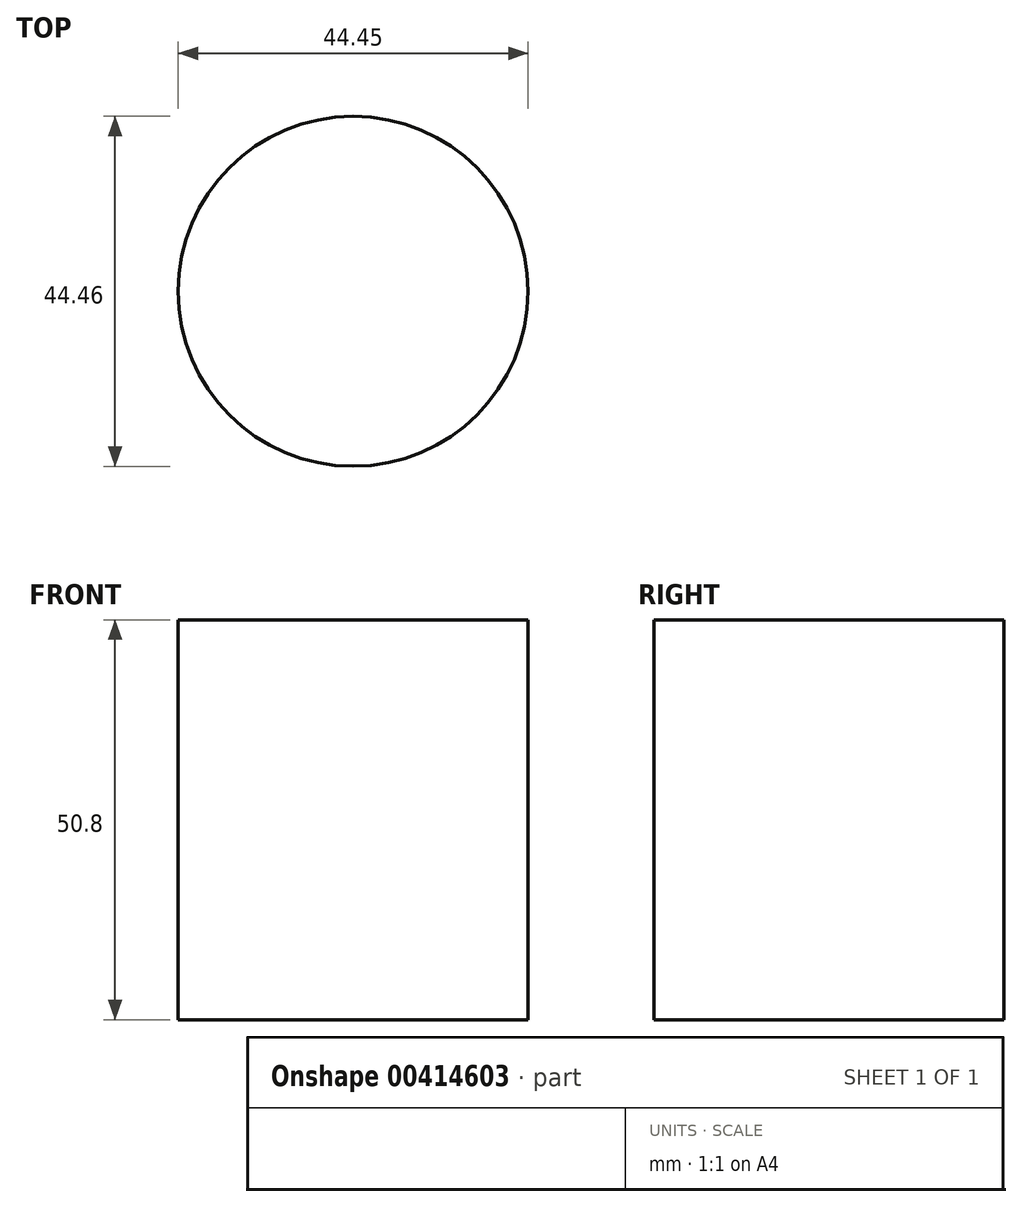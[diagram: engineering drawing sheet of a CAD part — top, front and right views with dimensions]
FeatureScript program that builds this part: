
annotation { "Feature Type Name" : "Feature", "Feature Type Description" : "" }
export const myFeature = defineFeature(function(context is Context, id is Id, definition is map)
    precondition{}
    {
        {
            var Q0;
            Q0=qCreatedBy(makeId("Top.planeOp"),FACE);
            var sketch = newSketch(context, id + "F0", { "sketchPlane" : qUnion([Q0])});
            skCircle(sketch, "E0", {"center": v(22.23, 0) * mm, "radius": 22.23 * mm});
            skSolve(sketch);
        }
        {
            var Q0;
            Q0 = qSketchRegion(id + "F0", true);
            extrude(context, id + "F1", {"entities" : qUnion([Q0]), "depth" : 50.8 * mm});
        }
    });
